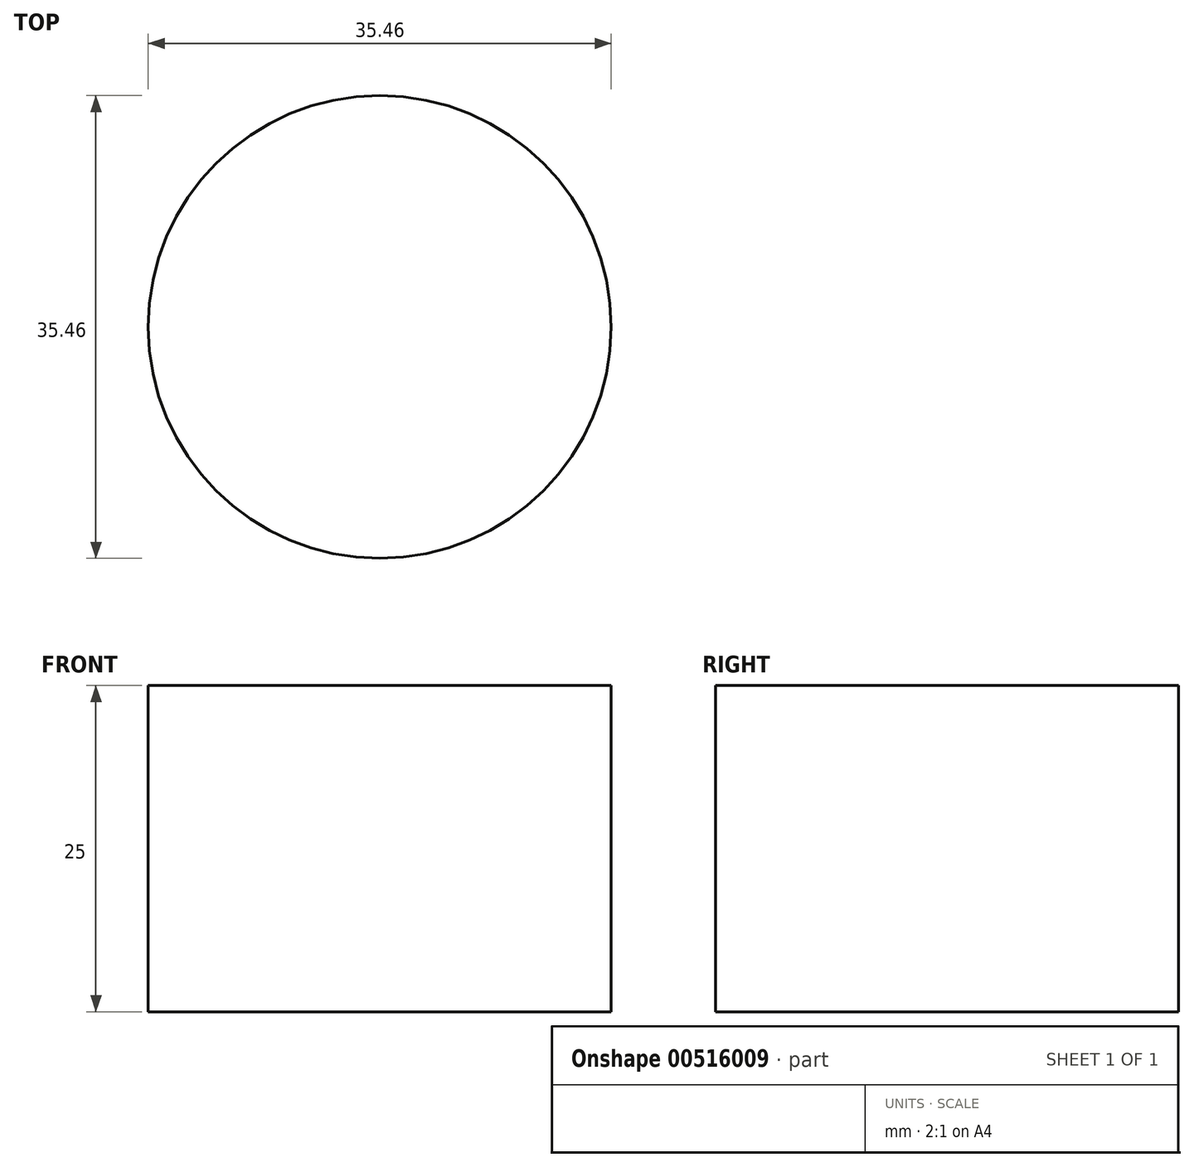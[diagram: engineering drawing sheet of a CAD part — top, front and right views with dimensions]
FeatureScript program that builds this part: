
annotation { "Feature Type Name" : "Feature", "Feature Type Description" : "" }
export const myFeature = defineFeature(function(context is Context, id is Id, definition is map)
    precondition{}
    {
        {
            var Q0;
            Q0=qCreatedBy(makeId("Top.planeOp"),FACE);
            var sketch = newSketch(context, id + "F0", { "sketchPlane" : qUnion([Q0])});
            skCircle(sketch, "E0", {"center": v(0, 0) * mm, "radius": 17.73 * mm});
            skSolve(sketch);
        }
        {
            var Q0;
            Q0 = qSketchRegion(id + "F0", true);
            extrude(context, id + "F1", {"entities" : qUnion([Q0]), "depth" : 25 * mm, "offsetDistance" : 25 * mm});
        }
    });
